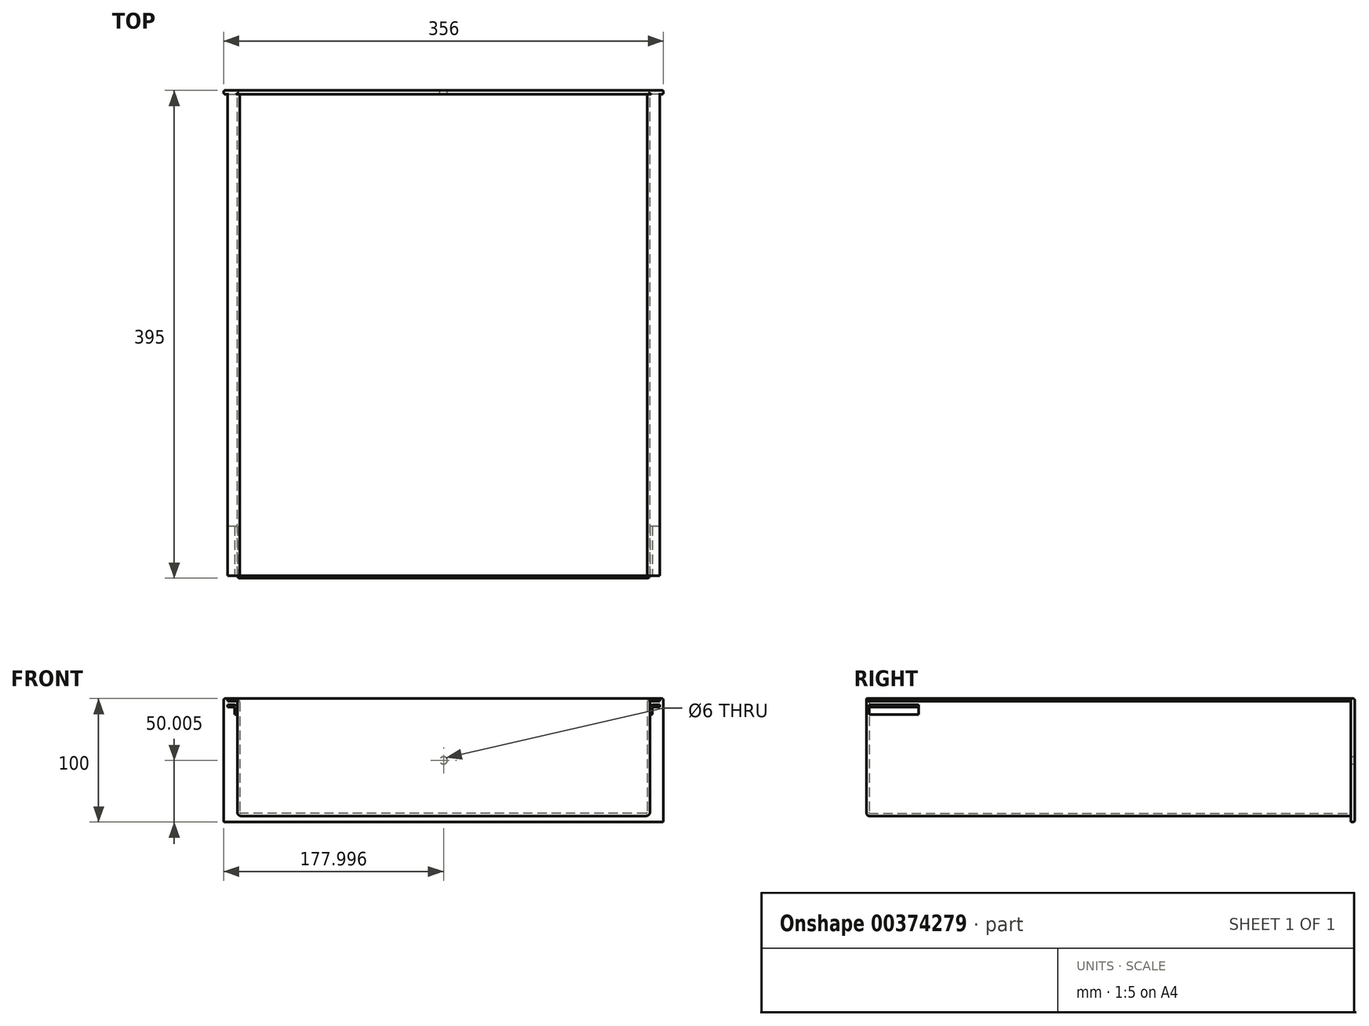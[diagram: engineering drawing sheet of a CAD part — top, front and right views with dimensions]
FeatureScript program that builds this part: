
annotation { "Feature Type Name" : "Feature", "Feature Type Description" : "" }
export const myFeature = defineFeature(function(context is Context, id is Id, definition is map)
    precondition{}
    {
        {
            var Q0;
            Q0=qCreatedBy(makeId("Front.planeOp"),FACE);
            var sketch = newSketch(context, id + "F0", { "sketchPlane" : qUnion([Q0])});
            skLineSegment(sketch, "E0.bottom", {"start": v(-164.5, 49.77) * mm, "end": v(191.5, 49.77) * mm});
            skLineSegment(sketch, "E0.top", {"start": v(-164.5, -50.23) * mm, "end": v(191.5, -50.23) * mm});
            skLineSegment(sketch, "E0.left", {"start": v(-164.5, 49.77) * mm, "end": v(-164.5, -50.23) * mm});
            skLineSegment(sketch, "E0.right", {"start": v(191.5, 49.77) * mm, "end": v(191.5, -50.23) * mm});
            skCircle(sketch, "E1", {"center": v(13.5, -0.23) * mm, "radius": 3 * mm});
            skSolve(sketch);
        }
        {
            var Q0;
            Q0 = qSketchRegion(id + "F0", true);
            extrude(context, id + "F1", {"entities" : qUnion([Q0]), "depth" : 3 * mm});
        }
        {
            var Q0;
            Q0=makeQuery(id+"F1.opExtrude","CAP_FACE",FACE,{"disambiguationData":[OSD([sQuery(id+"F0.wireOp",EDGE,"E0.bottom"),sQuery(id+"F0.wireOp",EDGE,"E0.top"),sQuery(id+"F0.wireOp",EDGE,"E0.left"),sQuery(id+"F0.wireOp",EDGE,"E0.right")])],"isStart":false});
            var sketch = newSketch(context, id + "F2", { "sketchPlane" : qUnion([Q0])});
            skLineSegment(sketch, "E2", {"start": v(-161.5, 47.77) * mm, "end": v(-153.5, 47.77) * mm});
            skLineSegment(sketch, "E3", {"start": v(-153.5, 47.77) * mm, "end": v(-153.5, -45.23) * mm});
            skLineSegment(sketch, "E4", {"start": v(-153.5, -45.23) * mm, "end": v(13.5, -45.23) * mm});
            skPoint(sketch, "E4.endSnap0", {"position": v(13.5, -50.23) * mm});
            skLineSegment(sketch, "E5", {"start": v(13.5, -50.23) * mm, "end": v(13.5, 49.77) * mm, "construction": true});
            skLineSegment(sketch, "E6.MirrorCS", {"start": v(180.5, -45.23) * mm, "end": v(13.5, -45.23) * mm});
            skLineSegment(sketch, "E7.MirrorCS", {"start": v(180.5, 47.77) * mm, "end": v(180.5, -45.23) * mm});
            skLineSegment(sketch, "E8.MirrorCS", {"start": v(188.5, 47.77) * mm, "end": v(180.5, 47.77) * mm});
            skLineSegment(sketch, "E9.0", {"start": v(188.5, 49.77) * mm, "end": v(178.5, 49.77) * mm});
            skLineSegment(sketch, "E9.1", {"start": v(178.5, 49.77) * mm, "end": v(178.5, -43.23) * mm});
            skLineSegment(sketch, "E9.2", {"start": v(-161.5, 49.77) * mm, "end": v(-151.5, 49.77) * mm});
            skLineSegment(sketch, "E9.3", {"start": v(-151.5, 49.77) * mm, "end": v(-151.5, -43.23) * mm});
            skLineSegment(sketch, "E9.4", {"start": v(-151.5, -43.23) * mm, "end": v(3.5, -43.23) * mm});
            skLineSegment(sketch, "E9.5", {"start": v(178.5, -43.23) * mm, "end": v(3.5, -43.23) * mm});
            skLineSegment(sketch, "E10", {"start": v(-161.5, 47.77) * mm, "end": v(-161.5, 49.77) * mm});
            skLineSegment(sketch, "E11", {"start": v(188.5, 47.77) * mm, "end": v(188.5, 49.77) * mm});
            skSolve(sketch);
        }
        {
            var Q0;
            Q0 = qSketchRegion(id + "F2", true);
            extrude(context, id + "F3", {"entities" : qUnion([Q0]), "operationType" : NewBodyOperationType.ADD, "depth" : 390 * mm});
        }
        {
            var Q0;
            Q0=makeQuery(id+"F3.opExtrude","CAP_FACE",FACE,{"disambiguationData":[OSD([sQuery(id+"F2.wireOp",EDGE,"E2"),sQuery(id+"F2.wireOp",EDGE,"E3"),sQuery(id+"F2.wireOp",EDGE,"E4"),sQuery(id+"F2.wireOp",EDGE,"E6.MirrorCS"),sQuery(id+"F2.wireOp",EDGE,"E7.MirrorCS"),sQuery(id+"F2.wireOp",EDGE,"E8.MirrorCS"),sQuery(id+"F2.wireOp",EDGE,"E9.0"),sQuery(id+"F2.wireOp",EDGE,"E9.1"),sQuery(id+"F2.wireOp",EDGE,"E9.2"),sQuery(id+"F2.wireOp",EDGE,"E9.3"),sQuery(id+"F2.wireOp",EDGE,"E9.4"),sQuery(id+"F2.wireOp",EDGE,"E9.5"),sQuery(id+"F2.wireOp",EDGE,"E10"),sQuery(id+"F2.wireOp",EDGE,"E11")])],"isStart":false});
            var sketch = newSketch(context, id + "F4", { "sketchPlane" : qUnion([Q0])});
            skLineSegment(sketch, "E12.bottom", {"start": v(-153.5, 49.77) * mm, "end": v(180.5, 49.77) * mm});
            skLineSegment(sketch, "E12.top", {"start": v(-153.5, -45.23) * mm, "end": v(180.5, -45.23) * mm});
            skLineSegment(sketch, "E12.left", {"start": v(-153.5, 49.77) * mm, "end": v(-153.5, -45.23) * mm});
            skLineSegment(sketch, "E12.right", {"start": v(180.5, 49.77) * mm, "end": v(180.5, -45.23) * mm});
            skLineSegment(sketch, "E13", {"start": v(182.5, 36.77) * mm, "end": v(180.5, 36.77) * mm});
            skLineSegment(sketch, "E14", {"start": v(180.5, 36.77) * mm, "end": v(180.5, 41.97) * mm});
            skLineSegment(sketch, "E15", {"start": v(183.3, 44.77) * mm, "end": v(188.5, 44.77) * mm});
            skLineSegment(sketch, "E16", {"start": v(188.5, 44.77) * mm, "end": v(188.5, 42.77) * mm});
            skLineSegment(sketch, "E17", {"start": v(188.5, 42.77) * mm, "end": v(183.3, 42.77) * mm});
            skLineSegment(sketch, "E18", {"start": v(182.5, 41.97) * mm, "end": v(182.5, 36.77) * mm});
            skLineSegment(sketch, "E19", {"start": v(13.5, -43.23) * mm, "end": v(13.5, 40.9) * mm});
            skLineSegment(sketch, "E20.MirrorCS", {"start": v(-155.5, 41.97) * mm, "end": v(-155.5, 36.77) * mm});
            skLineSegment(sketch, "E21.MirrorCS", {"start": v(-155.5, 36.77) * mm, "end": v(-153.5, 36.77) * mm});
            skLineSegment(sketch, "E22.MirrorCS", {"start": v(-153.5, 36.77) * mm, "end": v(-153.5, 41.97) * mm});
            skLineSegment(sketch, "E23.MirrorCS", {"start": v(-156.3, 44.77) * mm, "end": v(-161.5, 44.77) * mm});
            skLineSegment(sketch, "E24.MirrorCS", {"start": v(-161.5, 42.77) * mm, "end": v(-156.3, 42.77) * mm});
            skLineSegment(sketch, "E25.MirrorCS", {"start": v(-161.5, 44.77) * mm, "end": v(-161.5, 42.77) * mm});
            skPoint(sketch, "E26.visualSharp", {"position": v(182.5, 42.77) * mm});
            skArc(sketch, "E26.filletArc", {"start": v(183.3, 42.77) * mm, "mid": v(182.74, 42.54) * mm, "end": v(182.5, 41.97) * mm});
            skPoint(sketch, "E27.visualSharp", {"position": v(180.5, 44.77) * mm});
            skArc(sketch, "E27.filletArc", {"start": v(183.3, 44.77) * mm, "mid": v(181.33, 43.95) * mm, "end": v(180.5, 41.97) * mm});
            skPoint(sketch, "E28.visualSharp", {"position": v(-155.5, 42.77) * mm});
            skArc(sketch, "E28.filletArc", {"start": v(-155.5, 41.97) * mm, "mid": v(-155.73, 42.54) * mm, "end": v(-156.3, 42.77) * mm});
            skPoint(sketch, "E29.visualSharp", {"position": v(-153.5, 44.77) * mm});
            skArc(sketch, "E29.filletArc", {"start": v(-153.5, 41.97) * mm, "mid": v(-154.31, 43.95) * mm, "end": v(-156.3, 44.77) * mm});
            skSolve(sketch);
        }
        {
            var Q0;
            {var subQ1=sQuery(id+"F4.wireOp",EDGE,"E12.top");Q0=makeQuery(id+"F4.imprint","IMPRINT",FACE,{"disambiguationData":[TD([[makeQuery(id+"F4.imprint","IMPRINT",EDGE,{"derivedFrom":subQ1}),1.0]])]});}
            var Q1;
            {var subQ1=makeQuery(id+"F3.opExtrude","CAP_EDGE",EDGE,{"disambiguationData":[OSD([sQuery(id+"F2.wireOp",EDGE,"E9.1")])],"isStart":false});Q1=makeQuery(id+"F4.imprint","IMPRINT",FACE,{"disambiguationData":[TD([[makeQuery(id+"F4.imprint","IMPRINT",EDGE,{"derivedFrom":subQ1}),-1.0]])]});}
            extrude(context, id + "F5", {"entities" : qUnion([Q0, Q1]), "operationType" : NewBodyOperationType.ADD, "depth" : 2 * mm});
        }
        {
            var Q0;
            Q0=makeQuery(id+"F5.opExtrude","CAP_EDGE",EDGE,{"disambiguationData":[OSD([sQuery(id+"F4.wireOp",EDGE,"E12.right")])],"isStart":false});
            var Q1;
            Q1=makeQuery(id+"F5.opExtrude","CAP_EDGE",EDGE,{"disambiguationData":[OSD([sQuery(id+"F4.wireOp",EDGE,"E12.top")])],"isStart":false});
            var Q2;
            Q2=makeQuery(id+"F5.opExtrude","CAP_EDGE",EDGE,{"disambiguationData":[OSD([sQuery(id+"F4.wireOp",EDGE,"E12.left")])],"isStart":false});
            fillet(context, id + "F6", {"entities" : qUnion([Q0, Q1, Q2]), "radius" : 2 * mm, "tangentPropagation" : true, "allowEdgeOverflow" : false});
        }
        {
            var Q0;
            Q0=makeQuery(id+"F5.boolean.opBoolean","MERGE",EDGE,{"derivedFrom":[makeQuery(id+"F3.opExtrude","SWEPT_EDGE",EDGE,{"disambiguationData":[OSD([sQuery(id+"F2.wireOp",EDGE,"E6.MirrorCS"),sQuery(id+"F2.wireOp",EDGE,"E7.MirrorCS")])]}),makeQuery(id+"F5.opExtrude","SWEPT_EDGE",EDGE,{"disambiguationData":[OSD([sQuery(id+"F4.wireOp",EDGE,"E12.top"),sQuery(id+"F4.wireOp",EDGE,"E12.right")])]})]});
            var Q1;
            Q1=makeQuery(id+"F5.boolean.opBoolean","MERGE",EDGE,{"derivedFrom":[makeQuery(id+"F3.opExtrude","SWEPT_EDGE",EDGE,{"disambiguationData":[OSD([sQuery(id+"F2.wireOp",EDGE,"E3"),sQuery(id+"F2.wireOp",EDGE,"E4")])]}),makeQuery(id+"F5.opExtrude","SWEPT_EDGE",EDGE,{"disambiguationData":[OSD([sQuery(id+"F4.wireOp",EDGE,"E12.top"),sQuery(id+"F4.wireOp",EDGE,"E12.left")])]})]});
            var Q2;
            Q2=makeQuery(id+"F3.opExtrude","SWEPT_EDGE",EDGE,{"disambiguationData":[OSD([sQuery(id+"F0.wireOp",EDGE,"E0.bottom"),sQuery(id+"F2.wireOp",EDGE,"E9.2"),sQuery(id+"F2.wireOp",EDGE,"E9.3")])]});
            var Q3;
            Q3=makeQuery(id+"F3.opExtrude","SWEPT_EDGE",EDGE,{"disambiguationData":[OSD([sQuery(id+"F0.wireOp",EDGE,"E0.bottom"),sQuery(id+"F2.wireOp",EDGE,"E9.0"),sQuery(id+"F2.wireOp",EDGE,"E9.1")])]});
            fillet(context, id + "F7", {"entities" : qUnion([Q0, Q1, Q2, Q3]), "radius" : 3 * mm, "tangentPropagation" : true, "allowEdgeOverflow" : false});
        }
        {
            var Q0;
            Q0=makeQuery(id+"F3.opExtrude","SWEPT_EDGE",EDGE,{"disambiguationData":[OSD([sQuery(id+"F2.wireOp",EDGE,"E9.3"),sQuery(id+"F2.wireOp",EDGE,"E9.4")])]});
            var Q1;
            Q1=makeQuery(id+"F3.opExtrude","SWEPT_EDGE",EDGE,{"disambiguationData":[OSD([sQuery(id+"F2.wireOp",EDGE,"E2"),sQuery(id+"F2.wireOp",EDGE,"E3")])]});
            var Q2;
            Q2=makeQuery(id+"F3.opExtrude","SWEPT_EDGE",EDGE,{"disambiguationData":[OSD([sQuery(id+"F2.wireOp",EDGE,"E9.1"),sQuery(id+"F2.wireOp",EDGE,"E9.5")])]});
            var Q3;
            Q3=makeQuery(id+"F3.opExtrude","SWEPT_EDGE",EDGE,{"disambiguationData":[OSD([sQuery(id+"F2.wireOp",EDGE,"E7.MirrorCS"),sQuery(id+"F2.wireOp",EDGE,"E8.MirrorCS")])]});
            fillet(context, id + "F8", {"entities" : qUnion([Q0, Q1, Q2, Q3]), "radius" : 1 * mm, "tangentPropagation" : true, "allowEdgeOverflow" : false});
        }
        {
            var Q0;
            Q0=makeQuery(id+"F1.opExtrude","CAP_EDGE",EDGE,{"disambiguationData":[OSD([sQuery(id+"F0.wireOp",EDGE,"E0.left")])],"isStart":false});
            var Q1;
            {var subQ0=sQuery(id+"F0.wireOp",EDGE,"E0.left");var subQ1=sQuery(id+"F0.wireOp",EDGE,"E0.bottom");Q1=makeQuery(id+"F3.boolean.opBoolean","SPLIT",EDGE,{"disambiguationData":[TD([makeQuery(id+"F1.opExtrude","SWEPT_FACE",FACE,{"disambiguationData":[OSD([subQ0])]})])],"derivedFrom":makeQuery(id+"F1.opExtrude","CAP_EDGE",EDGE,{"disambiguationData":[OSD([subQ1])],"isStart":false})});}
            var Q2;
            {var subQ0=sQuery(id+"F0.wireOp",EDGE,"E0.bottom");Q2=makeQuery(id+"F3.boolean.opBoolean","SPLIT",EDGE,{"disambiguationData":[TD([makeQuery(id+"F3.opExtrude","SWEPT_FACE",FACE,{"disambiguationData":[OSD([sQuery(id+"F2.wireOp",EDGE,"E9.1")])]})])],"derivedFrom":makeQuery(id+"F1.opExtrude","CAP_EDGE",EDGE,{"disambiguationData":[OSD([subQ0])],"isStart":false})});}
            var Q3;
            Q3=makeQuery(id+"F1.opExtrude","CAP_EDGE",EDGE,{"disambiguationData":[OSD([sQuery(id+"F0.wireOp",EDGE,"E0.top")])],"isStart":false});
            var Q4;
            Q4=makeQuery(id+"F1.opExtrude","CAP_FACE",FACE,{"disambiguationData":[OSD([sQuery(id+"F0.wireOp",EDGE,"E0.bottom"),sQuery(id+"F0.wireOp",EDGE,"E0.top"),sQuery(id+"F0.wireOp",EDGE,"E0.left"),sQuery(id+"F0.wireOp",EDGE,"E0.right")])],"isStart":true});
            var Q5;
            Q5=makeQuery(id+"F1.opExtrude","CAP_EDGE",EDGE,{"disambiguationData":[OSD([sQuery(id+"F0.wireOp",EDGE,"E0.right")])],"isStart":false});
            var Q6;
            {var subQ0=sQuery(id+"F0.wireOp",EDGE,"E0.right");var subQ1=sQuery(id+"F0.wireOp",EDGE,"E0.bottom");Q6=makeQuery(id+"F3.boolean.opBoolean","SPLIT",EDGE,{"disambiguationData":[TD([makeQuery(id+"F1.opExtrude","SWEPT_FACE",FACE,{"disambiguationData":[OSD([subQ0])]})])],"derivedFrom":makeQuery(id+"F1.opExtrude","CAP_EDGE",EDGE,{"disambiguationData":[OSD([subQ1])],"isStart":false})});}
            var Q7;
            Q7=makeQuery(id+"F1.opExtrude","SWEPT_EDGE",EDGE,{"disambiguationData":[OSD([sQuery(id+"F0.wireOp",EDGE,"E0.bottom"),sQuery(id+"F0.wireOp",EDGE,"E0.right")])]});
            var Q8;
            Q8=makeQuery(id+"F1.opExtrude","SWEPT_EDGE",EDGE,{"disambiguationData":[OSD([sQuery(id+"F0.wireOp",EDGE,"E0.top"),sQuery(id+"F0.wireOp",EDGE,"E0.right")])]});
            var Q9;
            Q9=makeQuery(id+"F1.opExtrude","SWEPT_EDGE",EDGE,{"disambiguationData":[OSD([sQuery(id+"F0.wireOp",EDGE,"E0.top"),sQuery(id+"F0.wireOp",EDGE,"E0.left")])]});
            var Q10;
            Q10=makeQuery(id+"F1.opExtrude","SWEPT_EDGE",EDGE,{"disambiguationData":[OSD([sQuery(id+"F0.wireOp",EDGE,"E0.bottom"),sQuery(id+"F0.wireOp",EDGE,"E0.left")])]});
            fillet(context, id + "F9", {"entities" : qUnion([Q0, Q1, Q2, Q3, Q4, Q5, Q6, Q7, Q8, Q9, Q10]), "radius" : 1 * mm, "tangentPropagation" : true, "allowEdgeOverflow" : false});
        }
        {
            var Q0;
            Q0=makeQuery(id+"F4.imprint","IMPRINT",FACE,{"disambiguationData":[TD([[makeQuery(id+"F4.imprint","IMPRINT",EDGE,{"derivedFrom":sQuery(id+"F4.wireOp",EDGE,"E20.MirrorCS")}),1.0]])]});
            var Q1;
            Q1=makeQuery(id+"F4.imprint","IMPRINT",FACE,{"disambiguationData":[TD([[makeQuery(id+"F4.imprint","IMPRINT",EDGE,{"derivedFrom":sQuery(id+"F4.wireOp",EDGE,"E13")}),-1.0]])]});
            extrude(context, id + "F10", {"entities" : qUnion([Q0, Q1]), "oppositeDirection" : true, "depth" : 40 * mm});
        }
    });
